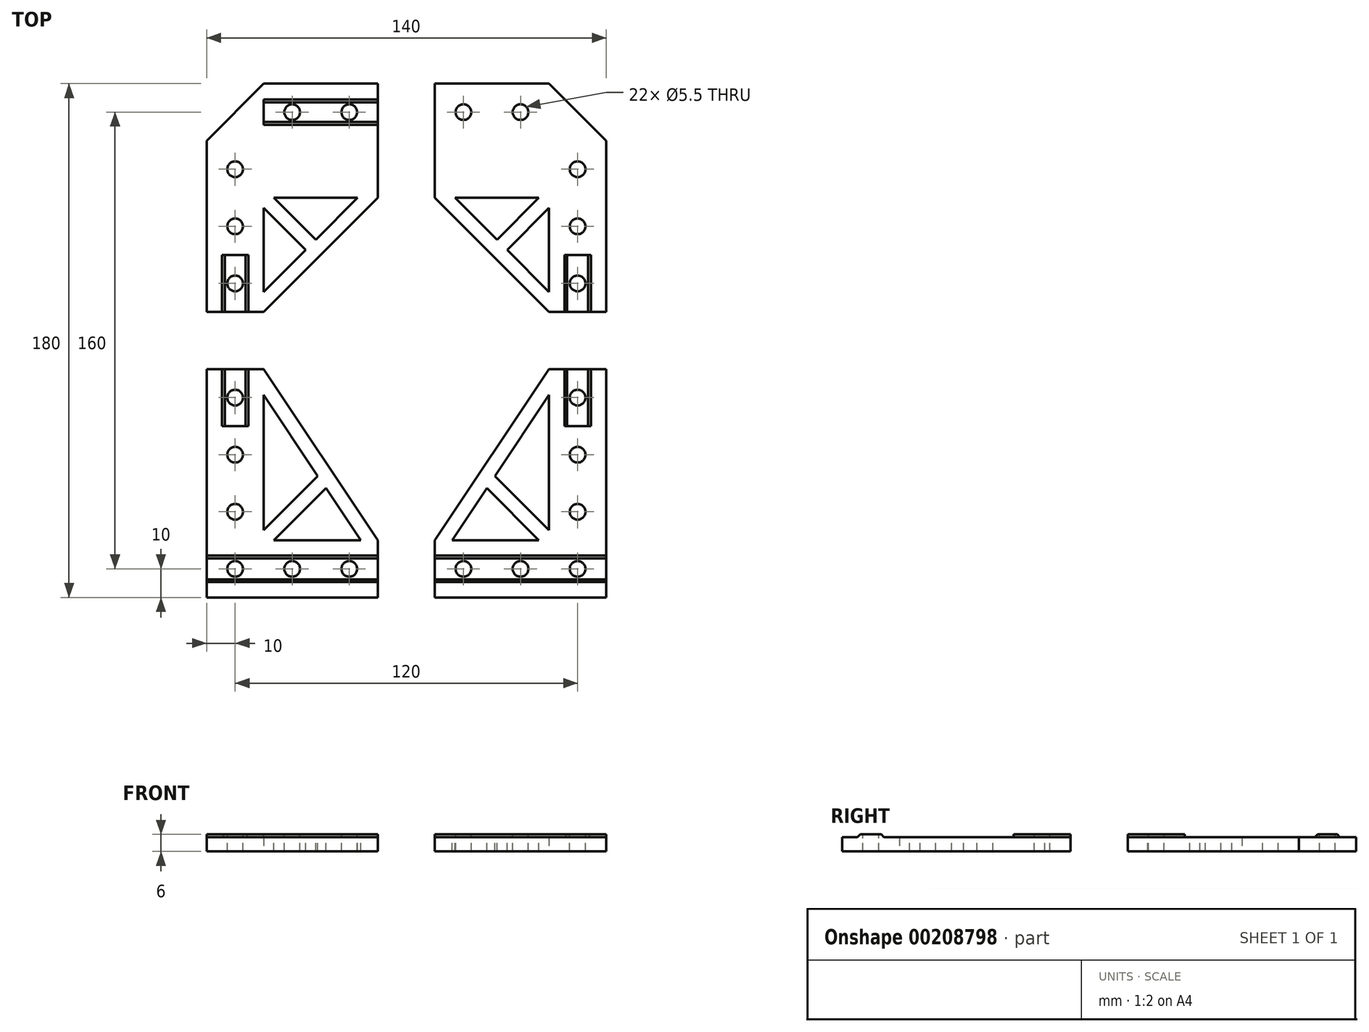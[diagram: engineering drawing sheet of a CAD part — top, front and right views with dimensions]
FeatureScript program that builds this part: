
annotation { "Feature Type Name" : "Feature", "Feature Type Description" : "" }
export const myFeature = defineFeature(function(context is Context, id is Id, definition is map)
    precondition{}
    {
        {
            var Q0;
            Q0=qCreatedBy(makeId("Top.planeOp"),FACE);
            var sketch = newSketch(context, id + "F0", { "sketchPlane" : qUnion([Q0])});
            skLineSegment(sketch, "E0", {"start": v(0, -60) * mm, "end": v(0, 0) * mm});
            skLineSegment(sketch, "E1", {"start": v(0, 0) * mm, "end": v(-20, 0) * mm, "construction": true});
            skLineSegment(sketch, "E2", {"start": v(-60, 0) * mm, "end": v(-60, -20) * mm});
            skLineSegment(sketch, "E3", {"start": v(-60, -20) * mm, "end": v(-20, -60) * mm});
            skLineSegment(sketch, "E4", {"start": v(-20, -60) * mm, "end": v(0, -60) * mm});
            skLineSegment(sketch, "E5", {"start": v(-60, 0) * mm, "end": v(-60, 20) * mm});
            skLineSegment(sketch, "E6", {"start": v(-60, 20) * mm, "end": v(-20, 20) * mm});
            skLineSegment(sketch, "E7", {"start": v(-20, 20) * mm, "end": v(-20, 0) * mm, "construction": true});
            skLineSegment(sketch, "E8", {"start": v(0, 0) * mm, "end": v(-20, 20) * mm});
            skLineSegment(sketch, "E9", {"start": v(-20, 10) * mm, "end": v(-30, 10) * mm, "construction": true});
            skLineSegment(sketch, "E10", {"start": v(-30, 10) * mm, "end": v(-50, 10) * mm, "construction": true});
            skLineSegment(sketch, "E11", {"start": v(-50, 10) * mm, "end": v(-60, 10) * mm, "construction": true});
            skLineSegment(sketch, "E12", {"start": v(-10, 0) * mm, "end": v(-10, -10) * mm, "construction": true});
            skPoint(sketch, "E12.endSnap0", {"position": v(-60, -10) * mm});
            skLineSegment(sketch, "E13", {"start": v(-10, -10) * mm, "end": v(-10, -30) * mm, "construction": true});
            skLineSegment(sketch, "E14", {"start": v(-10, -30) * mm, "end": v(-10, -50) * mm, "construction": true});
            skLineSegment(sketch, "E15", {"start": v(-10, -50) * mm, "end": v(-10, -60) * mm, "construction": true});
            skLineSegment(sketch, "E16", {"start": v(0, -80) * mm, "end": v(-20, -80) * mm});
            skLineSegment(sketch, "E17", {"start": v(-20, -80) * mm, "end": v(-60, -140) * mm});
            skLineSegment(sketch, "E18", {"start": v(-60, -140) * mm, "end": v(-60, -160) * mm});
            skLineSegment(sketch, "E19", {"start": v(-60, -160) * mm, "end": v(0, -160) * mm});
            skLineSegment(sketch, "E20", {"start": v(0, -160) * mm, "end": v(0, -80) * mm});
            skLineSegment(sketch, "E21", {"start": v(-60, -150) * mm, "end": v(-50, -150) * mm, "construction": true});
            skLineSegment(sketch, "E22", {"start": v(-50, -150) * mm, "end": v(-30, -150) * mm, "construction": true});
            skLineSegment(sketch, "E23", {"start": v(-30, -150) * mm, "end": v(-10, -150) * mm, "construction": true});
            skLineSegment(sketch, "E24", {"start": v(-10, -150) * mm, "end": v(0, -150) * mm, "construction": true});
            skLineSegment(sketch, "E25", {"start": v(-10, -80) * mm, "end": v(-10, -90) * mm, "construction": true});
            skLineSegment(sketch, "E26", {"start": v(-10, -90) * mm, "end": v(-10, -110) * mm, "construction": true});
            skLineSegment(sketch, "E27", {"start": v(-10, -110) * mm, "end": v(-10, -130) * mm, "construction": true});
            skLineSegment(sketch, "E28", {"start": v(-10, -130) * mm, "end": v(-10, -150) * mm, "construction": true});
            skLineSegment(sketch, "E29", {"start": v(-80, -160) * mm, "end": v(-80, -140) * mm});
            skLineSegment(sketch, "E30", {"start": v(-80, -140) * mm, "end": v(-120, -80) * mm});
            skLineSegment(sketch, "E31", {"start": v(-120, -80) * mm, "end": v(-140, -80) * mm});
            skLineSegment(sketch, "E32", {"start": v(-140, -80) * mm, "end": v(-140, -160) * mm});
            skLineSegment(sketch, "E33", {"start": v(-140, -160) * mm, "end": v(-80, -160) * mm});
            skLineSegment(sketch, "E34", {"start": v(-120, -60) * mm, "end": v(-140, -60) * mm});
            skLineSegment(sketch, "E35", {"start": v(-140, -60) * mm, "end": v(-140, 0) * mm});
            skLineSegment(sketch, "E36", {"start": v(-140, 0) * mm, "end": v(-120, 20) * mm});
            skLineSegment(sketch, "E37", {"start": v(-120, 20) * mm, "end": v(-80, 20) * mm});
            skLineSegment(sketch, "E38", {"start": v(-80, -20) * mm, "end": v(-120, -60) * mm});
            skLineSegment(sketch, "E39", {"start": v(-80, 20) * mm, "end": v(-80, 0) * mm});
            skLineSegment(sketch, "E40", {"start": v(-80, 0) * mm, "end": v(-80, -20) * mm});
            skLineSegment(sketch, "E41", {"start": v(-140, 0) * mm, "end": v(-120, 0) * mm, "construction": true});
            skLineSegment(sketch, "E42", {"start": v(-120, 0) * mm, "end": v(-120, 20) * mm, "construction": true});
            skLineSegment(sketch, "E43", {"start": v(-120, 10) * mm, "end": v(-110, 10) * mm, "construction": true});
            skLineSegment(sketch, "E44", {"start": v(-110, 10) * mm, "end": v(-90, 10) * mm, "construction": true});
            skLineSegment(sketch, "E45", {"start": v(-90, 10) * mm, "end": v(-80, 10) * mm, "construction": true});
            skLineSegment(sketch, "E46", {"start": v(-130, -10) * mm, "end": v(-130, -30) * mm, "construction": true});
            skLineSegment(sketch, "E47", {"start": v(-130, -30) * mm, "end": v(-130, -50) * mm, "construction": true});
            skLineSegment(sketch, "E48", {"start": v(-130, -50) * mm, "end": v(-130, -60) * mm, "construction": true});
            skLineSegment(sketch, "E49", {"start": v(-80, -150) * mm, "end": v(-90, -150) * mm, "construction": true});
            skLineSegment(sketch, "E50", {"start": v(-90, -150) * mm, "end": v(-110, -150) * mm, "construction": true});
            skLineSegment(sketch, "E51", {"start": v(-110, -150) * mm, "end": v(-130, -150) * mm, "construction": true});
            skLineSegment(sketch, "E52", {"start": v(-130, -150) * mm, "end": v(-130, -130) * mm, "construction": true});
            skLineSegment(sketch, "E53", {"start": v(-130, -130) * mm, "end": v(-130, -110) * mm, "construction": true});
            skLineSegment(sketch, "E54", {"start": v(-130, -110) * mm, "end": v(-130, -90) * mm, "construction": true});
            skLineSegment(sketch, "E55", {"start": v(-130, -90) * mm, "end": v(-130, -80) * mm, "construction": true});
            skLineSegment(sketch, "E56", {"start": v(-130, -10) * mm, "end": v(-130, 0) * mm});
            skSolve(sketch);
        }
        {
            var Q0;
            Q0=makeQuery(id+"F0.imprint","IMPRINT",FACE,{"disambiguationData":[TD([[makeQuery(id+"F0.imprint","IMPRINT",EDGE,{"derivedFrom":sQuery(id+"F0.wireOp",EDGE,"E0")}),1.0]])]});
            var Q1;
            Q1=makeQuery(id+"F0.imprint","IMPRINT",FACE,{"disambiguationData":[TD([[makeQuery(id+"F0.imprint","IMPRINT",EDGE,{"derivedFrom":sQuery(id+"F0.wireOp",EDGE,"E16")}),1.0]])]});
            var Q2;
            Q2=makeQuery(id+"F0.imprint","IMPRINT",FACE,{"disambiguationData":[TD([[makeQuery(id+"F0.imprint","IMPRINT",EDGE,{"derivedFrom":sQuery(id+"F0.wireOp",EDGE,"E34")}),-1.0]])]});
            var Q3;
            Q3=makeQuery(id+"F0.imprint","IMPRINT",FACE,{"disambiguationData":[TD([[makeQuery(id+"F0.imprint","IMPRINT",EDGE,{"derivedFrom":sQuery(id+"F0.wireOp",EDGE,"E29")}),1.0]])]});
            extrude(context, id + "F1", {"entities" : qUnion([Q0, Q1, Q2, Q3]), "depth" : 5 * mm});
        }
        {
            var Q0;
            Q0=makeQuery(id+"F1.opExtrude","CAP_FACE",FACE,{"disambiguationData":[OSD([sQuery(id+"F0.wireOp",EDGE,"E0"),sQuery(id+"F0.wireOp",EDGE,"E2"),sQuery(id+"F0.wireOp",EDGE,"E3"),sQuery(id+"F0.wireOp",EDGE,"E4"),sQuery(id+"F0.wireOp",EDGE,"E5"),sQuery(id+"F0.wireOp",EDGE,"E6"),sQuery(id+"F0.wireOp",EDGE,"E8")])],"isStart":false});
            var sketch = newSketch(context, id + "F2", { "sketchPlane" : qUnion([Q0])});
            skLineSegment(sketch, "E57", {"start": v(-23.54, -20) * mm, "end": v(-52.93, -20) * mm});
            skLineSegment(sketch, "E58", {"start": v(-52.93, -20) * mm, "end": v(-38.23, -34.7) * mm});
            skLineSegment(sketch, "E59", {"start": v(-38.23, -34.7) * mm, "end": v(-23.54, -20) * mm});
            skLineSegment(sketch, "E60", {"start": v(-20, -23.54) * mm, "end": v(-34.7, -38.23) * mm});
            skLineSegment(sketch, "E61", {"start": v(-34.7, -38.23) * mm, "end": v(-20, -52.93) * mm});
            skLineSegment(sketch, "E62", {"start": v(-20, -52.93) * mm, "end": v(-20, -23.54) * mm});
            skLineSegment(sketch, "E63", {"start": v(-23.54, -20) * mm, "end": v(-20, -20) * mm, "construction": true});
            skLineSegment(sketch, "E64", {"start": v(-20, -20) * mm, "end": v(-20, -23.54) * mm, "construction": true});
            skSolve(sketch);
        }
        {
            var Q0;
            Q0=makeQuery(id+"F2.imprint","IMPRINT",FACE,{"disambiguationData":[TD([[makeQuery(id+"F2.imprint","IMPRINT",EDGE,{"derivedFrom":sQuery(id+"F2.wireOp",EDGE,"E57")}),1.0]])]});
            var Q1;
            Q1=makeQuery(id+"F2.imprint","IMPRINT",FACE,{"disambiguationData":[TD([[makeQuery(id+"F2.imprint","IMPRINT",EDGE,{"derivedFrom":sQuery(id+"F2.wireOp",EDGE,"E60")}),1.0]])]});
            var Q2;
            Q2=sQuery(id+"F2.wireOp",EDGE,"YBFqt27e-qfMf-Dqdc-nEIm-QrJc93Nj7R85");
            var Q3;
            Q3=sQuery(id+"F2.wireOp",EDGE,"gDKsQo0I-stO4-j41u-VVKn-dd11EjwDGm8N");
            extrude(context, id + "F3", {"entities" : qUnion([Q0, Q1]), "operationType" : NewBodyOperationType.REMOVE, "surfaceEntities" : qUnion([Q2, Q3]), "endBound" : BoundingType.THROUGH_ALL, "oppositeDirection" : true, "depth" : 25 * mm});
        }
        {
            var Q0;
            Q0=makeQuery(id+"F1.opExtrude","SWEPT_FACE",FACE,{"disambiguationData":[OSD([sQuery(id+"F0.wireOp",EDGE,"E4")])]});
            var sketch = newSketch(context, id + "F4", { "sketchPlane" : qUnion([Q0])});
            skLineSegment(sketch, "E65", {"start": v(-20, 5) * mm, "end": v(-14.64, 5) * mm, "construction": true});
            skLineSegment(sketch, "E66", {"start": v(-14.64, 5) * mm, "end": v(-5.36, 5) * mm});
            skLineSegment(sketch, "E67", {"start": v(-5.36, 5) * mm, "end": v(0, 5) * mm, "construction": true});
            skLineSegment(sketch, "E68", {"start": v(-6.36, 6) * mm, "end": v(-5.36, 5) * mm});
            skLineSegment(sketch, "E69", {"start": v(-7.16, 6.8) * mm, "end": v(-6.36, 6) * mm, "construction": true});
            skLineSegment(sketch, "E70", {"start": v(-10, 9.64) * mm, "end": v(-7.16, 6.8) * mm, "construction": true});
            skLineSegment(sketch, "E71", {"start": v(-12.84, 6.8) * mm, "end": v(-10, 9.64) * mm, "construction": true});
            skLineSegment(sketch, "E72", {"start": v(-13.64, 6) * mm, "end": v(-12.84, 6.8) * mm, "construction": true});
            skLineSegment(sketch, "E73", {"start": v(-14.64, 5) * mm, "end": v(-13.64, 6) * mm});
            skLineSegment(sketch, "E74", {"start": v(-13.64, 6) * mm, "end": v(-6.36, 6) * mm});
            skLineSegment(sketch, "E75", {"start": v(-12.84, 6.8) * mm, "end": v(-7.16, 6.8) * mm, "construction": true});
            skLineSegment(sketch, "E76", {"start": v(-10, 6) * mm, "end": v(-10, 5) * mm, "construction": true});
            skSolve(sketch);
        }
        {
            var Q0;
            Q0=makeQuery(id+"F4.imprint","IMPRINT",FACE,{"disambiguationData":[TD([[makeQuery(id+"F4.imprint","IMPRINT",EDGE,{"derivedFrom":sQuery(id+"F4.wireOp",EDGE,"E66")}),1.0]])]});
            var Q1;
            Q1=sQuery(id+"F4.wireOp",EDGE,"E71");
            var Q2;
            Q2=sQuery(id+"F4.wireOp",EDGE,"E70");
            var Q3;
            Q3=sQuery(id+"F4.wireOp",EDGE,"E67");
            var Q4;
            Q4=sQuery(id+"F4.wireOp",EDGE,"E65");
            var Q5;
            Q5=sQuery(id+"F4.wireOp",EDGE,"E72");
            var Q6;
            Q6=sQuery(id+"F4.wireOp",EDGE,"E75");
            var Q7;
            Q7=sQuery(id+"F4.wireOp",EDGE,"E69");
            var Q8;
            Q8=sQuery(id+"F4.wireOp",EDGE,"E76");
            var Q9;
            Q9=makeQuery(id+"F1.opExtrude","SWEPT_FACE",FACE,{"disambiguationData":[OSD([sQuery(id+"F0.wireOp",EDGE,"E8")])]});
            extrude(context, id + "F5", {"entities" : qUnion([Q0]), "operationType" : NewBodyOperationType.ADD, "surfaceEntities" : qUnion([Q1, Q2, Q3, Q4, Q5, Q6, Q7, Q8]), "oppositeDirection" : true, "endBoundEntityFace" : qUnion([Q9]), "depth" : 20 * mm});
        }
        {
            var Q0;
            Q0=makeQuery(id+"F1.opExtrude","SWEPT_FACE",FACE,{"disambiguationData":[OSD([sQuery(id+"F0.wireOp",EDGE,"E2"),sQuery(id+"F0.wireOp",EDGE,"E5")])]});
            var sketch = newSketch(context, id + "F6", { "sketchPlane" : qUnion([Q0])});
            skLineSegment(sketch, "E77", {"start": v(-20, 5) * mm, "end": v(-14.64, 5) * mm, "construction": true});
            skLineSegment(sketch, "E78", {"start": v(-14.64, 5) * mm, "end": v(-5.36, 5) * mm});
            skLineSegment(sketch, "E79", {"start": v(-5.36, 5) * mm, "end": v(-6.36, 6) * mm});
            skLineSegment(sketch, "E80", {"start": v(-6.36, 6) * mm, "end": v(-7.16, 6.8) * mm, "construction": true});
            skLineSegment(sketch, "E81", {"start": v(-7.16, 6.8) * mm, "end": v(-10, 9.64) * mm, "construction": true});
            skLineSegment(sketch, "E82", {"start": v(-10, 9.64) * mm, "end": v(-12.84, 6.8) * mm, "construction": true});
            skLineSegment(sketch, "E83", {"start": v(-12.84, 6.8) * mm, "end": v(-13.64, 6) * mm, "construction": true});
            skLineSegment(sketch, "E84", {"start": v(-13.64, 6) * mm, "end": v(-14.64, 5) * mm});
            skLineSegment(sketch, "E85", {"start": v(-6.36, 6) * mm, "end": v(-13.64, 6) * mm});
            skLineSegment(sketch, "E86", {"start": v(-12.84, 6.8) * mm, "end": v(-7.16, 6.8) * mm, "construction": true});
            skLineSegment(sketch, "E87", {"start": v(-10, 6) * mm, "end": v(-10, 5) * mm, "construction": true});
            skSolve(sketch);
        }
        {
            var Q0;
            Q0=makeQuery(id+"F6.imprint","IMPRINT",FACE,{"disambiguationData":[TD([[makeQuery(id+"F6.imprint","IMPRINT",EDGE,{"derivedFrom":sQuery(id+"F6.wireOp",EDGE,"E78")}),-1.0]])]});
            var Q1;
            Q1=sQuery(id+"F6.wireOp",EDGE,"E82");
            var Q2;
            Q2=sQuery(id+"F6.wireOp",EDGE,"E81");
            var Q3;
            Q3=sQuery(id+"F6.wireOp",EDGE,"E86");
            var Q4;
            Q4=sQuery(id+"F6.wireOp",EDGE,"E80");
            var Q5;
            Q5=sQuery(id+"F6.wireOp",EDGE,"E83");
            var Q6;
            Q6=sQuery(id+"F6.wireOp",EDGE,"E77");
            var Q7;
            Q7=sQuery(id+"F6.wireOp",EDGE,"E87");
            extrude(context, id + "F7", {"entities" : qUnion([Q0]), "operationType" : NewBodyOperationType.ADD, "surfaceEntities" : qUnion([Q1, Q2, Q3, Q4, Q5, Q6, Q7]), "oppositeDirection" : true, "depth" : 40 * mm});
        }
        {
            var Q0;
            Q0=makeQuery(id+"F1.opExtrude","SWEPT_FACE",FACE,{"disambiguationData":[OSD([sQuery(id+"F0.wireOp",EDGE,"E16")])]});
            var sketch = newSketch(context, id + "F8", { "sketchPlane" : qUnion([Q0])});
            skLineSegment(sketch, "E88", {"start": v(0, 5) * mm, "end": v(5.36, 5) * mm, "construction": true});
            skLineSegment(sketch, "E89", {"start": v(14.64, 5) * mm, "end": v(20, 5) * mm, "construction": true});
            skLineSegment(sketch, "E90", {"start": v(5.36, 5) * mm, "end": v(14.64, 5) * mm});
            skLineSegment(sketch, "E91", {"start": v(10, 5) * mm, "end": v(10, 0) * mm, "construction": true});
            skLineSegment(sketch, "E92", {"start": v(5.36, 5) * mm, "end": v(6.36, 6) * mm});
            skLineSegment(sketch, "E93", {"start": v(6.36, 6) * mm, "end": v(7.16, 6.8) * mm, "construction": true});
            skLineSegment(sketch, "E94", {"start": v(7.16, 6.8) * mm, "end": v(10, 9.64) * mm, "construction": true});
            skLineSegment(sketch, "E95", {"start": v(10, 9.64) * mm, "end": v(12.84, 6.8) * mm, "construction": true});
            skLineSegment(sketch, "E96", {"start": v(12.84, 6.8) * mm, "end": v(13.64, 6) * mm, "construction": true});
            skLineSegment(sketch, "E97", {"start": v(13.64, 6) * mm, "end": v(14.64, 5) * mm});
            skLineSegment(sketch, "E98", {"start": v(6.36, 6) * mm, "end": v(13.64, 6) * mm});
            skLineSegment(sketch, "E99", {"start": v(7.16, 6.8) * mm, "end": v(12.84, 6.8) * mm, "construction": true});
            skLineSegment(sketch, "E100", {"start": v(10, 5) * mm, "end": v(10, 6) * mm, "construction": true});
            skSolve(sketch);
        }
        {
            var Q0;
            Q0=qSketchRegion(id+"F8",true);
            var Q1;
            Q1=sQuery(id+"F8.wireOp",EDGE,"E100");
            var Q2;
            Q2=sQuery(id+"F8.wireOp",EDGE,"E88");
            var Q3;
            Q3=sQuery(id+"F8.wireOp",EDGE,"E91");
            var Q4;
            Q4=sQuery(id+"F8.wireOp",EDGE,"E89");
            var Q5;
            Q5=sQuery(id+"F8.wireOp",EDGE,"E96");
            var Q6;
            Q6=sQuery(id+"F8.wireOp",EDGE,"E99");
            var Q7;
            Q7=sQuery(id+"F8.wireOp",EDGE,"E95");
            var Q8;
            Q8=sQuery(id+"F8.wireOp",EDGE,"E94");
            var Q9;
            Q9=sQuery(id+"F8.wireOp",EDGE,"E93");
            extrude(context, id + "F9", {"entities" : qUnion([Q0]), "operationType" : NewBodyOperationType.ADD, "surfaceEntities" : qUnion([Q1, Q2, Q3, Q4, Q5, Q6, Q7, Q8, Q9]), "oppositeDirection" : true, "depth" : 20 * mm});
        }
        {
            var Q0;
            Q0=makeQuery(id+"F1.opExtrude","SWEPT_FACE",FACE,{"disambiguationData":[OSD([sQuery(id+"F0.wireOp",EDGE,"E20")])]});
            var sketch = newSketch(context, id + "F10", { "sketchPlane" : qUnion([Q0])});
            skLineSegment(sketch, "E101", {"start": v(-160, 5) * mm, "end": v(-154.64, 5) * mm, "construction": true});
            skLineSegment(sketch, "E102", {"start": v(-154.64, 5) * mm, "end": v(-145.36, 5) * mm});
            skLineSegment(sketch, "E103", {"start": v(-145.36, 5) * mm, "end": v(-140, 5) * mm, "construction": true});
            skLineSegment(sketch, "E104", {"start": v(-150, 5) * mm, "end": v(-150, 0) * mm, "construction": true});
            skLineSegment(sketch, "E105", {"start": v(-154.64, 5) * mm, "end": v(-153.64, 6) * mm});
            skLineSegment(sketch, "E106", {"start": v(-153.64, 6) * mm, "end": v(-152.84, 6.8) * mm, "construction": true});
            skLineSegment(sketch, "E107", {"start": v(-152.84, 6.8) * mm, "end": v(-150, 9.64) * mm, "construction": true});
            skLineSegment(sketch, "E108", {"start": v(-150, 9.64) * mm, "end": v(-147.16, 6.8) * mm, "construction": true});
            skLineSegment(sketch, "E109", {"start": v(-147.16, 6.8) * mm, "end": v(-146.36, 6) * mm, "construction": true});
            skLineSegment(sketch, "E110", {"start": v(-146.36, 6) * mm, "end": v(-145.36, 5) * mm});
            skLineSegment(sketch, "E111", {"start": v(-152.84, 6.8) * mm, "end": v(-147.16, 6.8) * mm, "construction": true});
            skLineSegment(sketch, "E112", {"start": v(-153.64, 6) * mm, "end": v(-146.36, 6) * mm});
            skLineSegment(sketch, "E113", {"start": v(-150, 6) * mm, "end": v(-150, 5) * mm, "construction": true});
            skSolve(sketch);
        }
        {
            var Q0;
            Q0=makeQuery(id+"F10.imprint","IMPRINT",FACE,{"disambiguationData":[TD([[makeQuery(id+"F10.imprint","IMPRINT",EDGE,{"derivedFrom":sQuery(id+"F10.wireOp",EDGE,"E102")}),1.0]])]});
            var Q1;
            Q1=makeQuery(id+"F1.opExtrude","SWEPT_FACE",FACE,{"disambiguationData":[OSD([sQuery(id+"F0.wireOp",EDGE,"E18")])]});
            extrude(context, id + "F11", {"entities" : qUnion([Q0]), "operationType" : NewBodyOperationType.ADD, "endBound" : BoundingType.UP_TO_SURFACE, "oppositeDirection" : true, "endBoundEntityFace" : qUnion([Q1]), "depth" : 25 * mm});
        }
        {
            var Q0;
            {var subQ4=sQuery(id+"F0.wireOp",EDGE,"E16");var subQ9=sQuery(id+"F0.wireOp",EDGE,"E17");var subQ10=sQuery(id+"F0.wireOp",EDGE,"E18");var subQ11=sQuery(id+"F0.wireOp",EDGE,"E20");Q0=makeQuery(id+"F11.boolean.opBoolean","SPLIT",FACE,{"disambiguationData":[TD([makeQuery(id+"F1.opExtrude","SWEPT_FACE",FACE,{"disambiguationData":[OSD([subQ4])]})])],"derivedFrom":makeQuery(id+"F1.opExtrude","CAP_FACE",FACE,{"disambiguationData":[OSD([subQ4,subQ9,subQ10,sQuery(id+"F0.wireOp",EDGE,"E19"),subQ11])],"isStart":false})});}
            var sketch = newSketch(context, id + "F12", { "sketchPlane" : qUnion([Q0])});
            skLineSegment(sketch, "E114", {"start": v(-54, -140) * mm, "end": v(-23.54, -140) * mm});
            skLineSegment(sketch, "E115", {"start": v(-23.54, -140) * mm, "end": v(-41.8, -121.73) * mm});
            skLineSegment(sketch, "E116", {"start": v(-41.8, -121.73) * mm, "end": v(-54, -140) * mm});
            skLineSegment(sketch, "E117", {"start": v(-20, -136.46) * mm, "end": v(-38.98, -117.48) * mm});
            skLineSegment(sketch, "E118", {"start": v(-38.98, -117.48) * mm, "end": v(-20, -89.01) * mm});
            skLineSegment(sketch, "E119", {"start": v(-20, -89.01) * mm, "end": v(-20, -136.46) * mm});
            skLineSegment(sketch, "E120", {"start": v(-23.54, -140) * mm, "end": v(-20, -140) * mm, "construction": true});
            skLineSegment(sketch, "E121", {"start": v(-20, -140) * mm, "end": v(-20, -136.46) * mm, "construction": true});
            skSolve(sketch);
        }
        {
            var Q0;
            Q0=makeQuery(id+"F12.imprint","IMPRINT",FACE,{"disambiguationData":[TD([[makeQuery(id+"F12.imprint","IMPRINT",EDGE,{"derivedFrom":sQuery(id+"F12.wireOp",EDGE,"E117")}),-1.0]])]});
            var Q1;
            Q1=makeQuery(id+"F12.imprint","IMPRINT",FACE,{"disambiguationData":[TD([[makeQuery(id+"F12.imprint","IMPRINT",EDGE,{"derivedFrom":sQuery(id+"F12.wireOp",EDGE,"E114")}),1.0]])]});
            extrude(context, id + "F13", {"entities" : qUnion([Q0, Q1]), "operationType" : NewBodyOperationType.REMOVE, "oppositeDirection" : true, "depth" : 25 * mm});
        }
        {
            var Q0;
            Q0=makeQuery(id+"F1.opExtrude","SWEPT_FACE",FACE,{"disambiguationData":[OSD([sQuery(id+"F0.wireOp",EDGE,"E32")])]});
            var sketch = newSketch(context, id + "F14", { "sketchPlane" : qUnion([Q0])});
            skLineSegment(sketch, "E122", {"start": v(145.36, 5) * mm, "end": v(154.64, 5) * mm});
            skLineSegment(sketch, "E123", {"start": v(154.64, 5) * mm, "end": v(153.64, 6) * mm});
            skLineSegment(sketch, "E124", {"start": v(153.64, 6) * mm, "end": v(152.84, 6.8) * mm, "construction": true});
            skLineSegment(sketch, "E125", {"start": v(152.84, 6.8) * mm, "end": v(150, 9.64) * mm, "construction": true});
            skLineSegment(sketch, "E126", {"start": v(150, 9.64) * mm, "end": v(147.16, 6.8) * mm, "construction": true});
            skLineSegment(sketch, "E127", {"start": v(147.16, 6.8) * mm, "end": v(146.36, 6) * mm, "construction": true});
            skLineSegment(sketch, "E128", {"start": v(146.36, 6) * mm, "end": v(145.36, 5) * mm});
            skLineSegment(sketch, "E129", {"start": v(146.36, 6) * mm, "end": v(153.64, 6) * mm});
            skLineSegment(sketch, "E130", {"start": v(152.84, 6.8) * mm, "end": v(147.16, 6.8) * mm, "construction": true});
            skLineSegment(sketch, "E131", {"start": v(150, 0) * mm, "end": v(150, 5) * mm, "construction": true});
            skLineSegment(sketch, "E132", {"start": v(150, 6) * mm, "end": v(150, 5) * mm, "construction": true});
            skSolve(sketch);
        }
        {
            var Q0;
            Q0=makeQuery(id+"F14.imprint","IMPRINT",FACE,{"disambiguationData":[TD([[makeQuery(id+"F14.imprint","IMPRINT",EDGE,{"derivedFrom":sQuery(id+"F14.wireOp",EDGE,"E122")}),1.0]])]});
            var Q1;
            Q1=makeQuery(id+"F1.opExtrude","SWEPT_FACE",FACE,{"disambiguationData":[OSD([sQuery(id+"F0.wireOp",EDGE,"E29")])]});
            extrude(context, id + "F15", {"entities" : qUnion([Q0]), "operationType" : NewBodyOperationType.ADD, "endBound" : BoundingType.UP_TO_SURFACE, "oppositeDirection" : true, "endBoundEntityFace" : qUnion([Q1]), "depth" : 25 * mm});
        }
        {
            var Q0;
            Q0=makeQuery(id+"F1.opExtrude","SWEPT_FACE",FACE,{"disambiguationData":[OSD([sQuery(id+"F0.wireOp",EDGE,"E31")])]});
            var sketch = newSketch(context, id + "F16", { "sketchPlane" : qUnion([Q0])});
            skLineSegment(sketch, "E133", {"start": v(134.64, 5) * mm, "end": v(125.36, 5) * mm});
            skLineSegment(sketch, "E134", {"start": v(125.36, 5) * mm, "end": v(126.36, 6) * mm});
            skLineSegment(sketch, "E135", {"start": v(126.36, 6) * mm, "end": v(127.16, 6.8) * mm, "construction": true});
            skLineSegment(sketch, "E136", {"start": v(127.16, 6.8) * mm, "end": v(130, 9.64) * mm, "construction": true});
            skLineSegment(sketch, "E137", {"start": v(130, 9.64) * mm, "end": v(132.84, 6.8) * mm, "construction": true});
            skLineSegment(sketch, "E138", {"start": v(132.84, 6.8) * mm, "end": v(133.64, 6) * mm, "construction": true});
            skLineSegment(sketch, "E139", {"start": v(133.64, 6) * mm, "end": v(134.64, 5) * mm});
            skLineSegment(sketch, "E140", {"start": v(130, 5) * mm, "end": v(130, 0) * mm, "construction": true});
            skLineSegment(sketch, "E141", {"start": v(126.36, 6) * mm, "end": v(133.64, 6) * mm});
            skLineSegment(sketch, "E142", {"start": v(132.84, 6.8) * mm, "end": v(127.16, 6.8) * mm, "construction": true});
            skLineSegment(sketch, "E143", {"start": v(130, 6) * mm, "end": v(130, 5) * mm, "construction": true});
            skSolve(sketch);
        }
        {
            var Q0;
            Q0=makeQuery(id+"F16.imprint","IMPRINT",FACE,{"disambiguationData":[TD([[makeQuery(id+"F16.imprint","IMPRINT",EDGE,{"derivedFrom":sQuery(id+"F16.wireOp",EDGE,"E133")}),1.0]])]});
            extrude(context, id + "F17", {"entities" : qUnion([Q0]), "operationType" : NewBodyOperationType.ADD, "oppositeDirection" : true, "depth" : 20 * mm});
        }
        {
            var Q0;
            Q0=makeQuery(id+"F1.opExtrude","SWEPT_FACE",FACE,{"disambiguationData":[OSD([sQuery(id+"F0.wireOp",EDGE,"E34")])]});
            var sketch = newSketch(context, id + "F18", { "sketchPlane" : qUnion([Q0])});
            skLineSegment(sketch, "E144", {"start": v(-134.64, 5) * mm, "end": v(-125.36, 5) * mm});
            skLineSegment(sketch, "E145", {"start": v(-125.36, 5) * mm, "end": v(-126.36, 6) * mm});
            skLineSegment(sketch, "E146", {"start": v(-126.36, 6) * mm, "end": v(-127.16, 6.8) * mm, "construction": true});
            skLineSegment(sketch, "E147", {"start": v(-127.16, 6.8) * mm, "end": v(-130, 9.64) * mm, "construction": true});
            skLineSegment(sketch, "E148", {"start": v(-130, 9.64) * mm, "end": v(-132.84, 6.8) * mm, "construction": true});
            skLineSegment(sketch, "E149", {"start": v(-132.84, 6.8) * mm, "end": v(-133.64, 6) * mm, "construction": true});
            skLineSegment(sketch, "E150", {"start": v(-133.64, 6) * mm, "end": v(-134.64, 5) * mm});
            skLineSegment(sketch, "E151", {"start": v(-127.16, 6.8) * mm, "end": v(-132.84, 6.8) * mm, "construction": true});
            skLineSegment(sketch, "E152", {"start": v(-133.64, 6) * mm, "end": v(-126.36, 6) * mm});
            skLineSegment(sketch, "E153", {"start": v(-130, 5) * mm, "end": v(-130, 6) * mm, "construction": true});
            skLineSegment(sketch, "E154", {"start": v(-130, 5) * mm, "end": v(-130, 0) * mm, "construction": true});
            skSolve(sketch);
        }
        {
            var Q0;
            Q0=makeQuery(id+"F18.imprint","IMPRINT",FACE,{"disambiguationData":[TD([[makeQuery(id+"F18.imprint","IMPRINT",EDGE,{"derivedFrom":sQuery(id+"F18.wireOp",EDGE,"E144")}),-1.0]])]});
            var Q1;
            Q1=sQuery(id+"F18.wireOp",EDGE,"E154");
            var Q2;
            Q2=sQuery(id+"F18.wireOp",EDGE,"E153");
            var Q3;
            Q3=sQuery(id+"F18.wireOp",EDGE,"E149");
            var Q4;
            Q4=sQuery(id+"F18.wireOp",EDGE,"E151");
            var Q5;
            Q5=sQuery(id+"F18.wireOp",EDGE,"E146");
            var Q6;
            Q6=sQuery(id+"F18.wireOp",EDGE,"E147");
            var Q7;
            Q7=sQuery(id+"F18.wireOp",EDGE,"E148");
            extrude(context, id + "F19", {"entities" : qUnion([Q0]), "operationType" : NewBodyOperationType.ADD, "surfaceEntities" : qUnion([Q1, Q2, Q3, Q4, Q5, Q6, Q7]), "oppositeDirection" : true, "depth" : 20 * mm});
        }
        {
            var Q0;
            Q0=makeQuery(id+"F1.opExtrude","SWEPT_FACE",FACE,{"disambiguationData":[OSD([sQuery(id+"F0.wireOp",EDGE,"E39"),sQuery(id+"F0.wireOp",EDGE,"E40")])]});
            var sketch = newSketch(context, id + "F20", { "sketchPlane" : qUnion([Q0])});
            skLineSegment(sketch, "E155", {"start": v(5.6, 5) * mm, "end": v(14.4, 5) * mm});
            skLineSegment(sketch, "E156", {"start": v(14.4, 5) * mm, "end": v(13.4, 6) * mm});
            skLineSegment(sketch, "E157", {"start": v(13.4, 6) * mm, "end": v(12.6, 6.8) * mm, "construction": true});
            skLineSegment(sketch, "E158", {"start": v(12.6, 6.8) * mm, "end": v(10, 9.4) * mm, "construction": true});
            skLineSegment(sketch, "E159", {"start": v(10, 9.4) * mm, "end": v(7.4, 6.8) * mm, "construction": true});
            skLineSegment(sketch, "E160", {"start": v(7.4, 6.8) * mm, "end": v(6.6, 6) * mm, "construction": true});
            skLineSegment(sketch, "E161", {"start": v(6.6, 6) * mm, "end": v(5.6, 5) * mm});
            skLineSegment(sketch, "E162", {"start": v(10, 5) * mm, "end": v(10, 0) * mm, "construction": true});
            skLineSegment(sketch, "E163", {"start": v(13.4, 6) * mm, "end": v(6.6, 6) * mm});
            skLineSegment(sketch, "E164", {"start": v(7.4, 6.8) * mm, "end": v(12.6, 6.8) * mm, "construction": true});
            skLineSegment(sketch, "E165", {"start": v(10, 6) * mm, "end": v(10, 5) * mm, "construction": true});
            skSolve(sketch);
        }
        {
            var Q0;
            Q0=makeQuery(id+"F20.imprint","IMPRINT",FACE,{"disambiguationData":[TD([[makeQuery(id+"F20.imprint","IMPRINT",EDGE,{"derivedFrom":sQuery(id+"F20.wireOp",EDGE,"E155")}),-1.0]])]});
            var Q1;
            Q1=sQuery(id+"F20.wireOp",EDGE,"E165");
            var Q2;
            Q2=sQuery(id+"F20.wireOp",EDGE,"E162");
            var Q3;
            Q3=sQuery(id+"F20.wireOp",EDGE,"E160");
            var Q4;
            Q4=sQuery(id+"F20.wireOp",EDGE,"E164");
            var Q5;
            Q5=sQuery(id+"F20.wireOp",EDGE,"E159");
            var Q6;
            Q6=sQuery(id+"F20.wireOp",EDGE,"E158");
            var Q7;
            Q7=sQuery(id+"F20.wireOp",EDGE,"E157");
            extrude(context, id + "F21", {"entities" : qUnion([Q0]), "operationType" : NewBodyOperationType.ADD, "surfaceEntities" : qUnion([Q1, Q2, Q3, Q4, Q5, Q6, Q7]), "oppositeDirection" : true, "depth" : 40 * mm});
        }
        {
            var Q0;
            Q0=sQuery(id+"F0.wireOp",VERTEX,"E44.start");
            var Q1;
            Q1=sQuery(id+"F0.wireOp",VERTEX,"E44.end");
            var Q2;
            Q2=sQuery(id+"F0.wireOp",VERTEX,"E11.start");
            var Q3;
            Q3=sQuery(id+"F0.wireOp",VERTEX,"E10.start");
            var Q4;
            Q4=sQuery(id+"F0.wireOp",VERTEX,"E46.start");
            var Q5;
            Q5=sQuery(id+"F0.wireOp",VERTEX,"E12.end");
            var Q6;
            Q6=sQuery(id+"F0.wireOp",VERTEX,"E14.start");
            var Q7;
            Q7=sQuery(id+"F0.wireOp",VERTEX,"E15.start");
            var Q8;
            Q8=sQuery(id+"F0.wireOp",VERTEX,"E47.end");
            var Q9;
            Q9=sQuery(id+"F0.wireOp",VERTEX,"E47.start");
            var Q10;
            Q10=sQuery(id+"F0.wireOp",VERTEX,"E52.end");
            var Q11;
            Q11=sQuery(id+"F0.wireOp",VERTEX,"E53.end");
            var Q12;
            Q12=sQuery(id+"F0.wireOp",VERTEX,"E55.start");
            var Q13;
            Q13=sQuery(id+"F0.wireOp",VERTEX,"E28.start");
            var Q14;
            Q14=sQuery(id+"F0.wireOp",VERTEX,"E27.start");
            var Q15;
            Q15=sQuery(id+"F0.wireOp",VERTEX,"E26.start");
            var Q16;
            Q16=sQuery(id+"F0.wireOp",VERTEX,"E52.start");
            var Q17;
            Q17=sQuery(id+"F0.wireOp",VERTEX,"E51.start");
            var Q18;
            Q18=sQuery(id+"F0.wireOp",VERTEX,"E50.start");
            var Q19;
            Q19=sQuery(id+"F0.wireOp",VERTEX,"E22.start");
            var Q20;
            Q20=sQuery(id+"F0.wireOp",VERTEX,"E23.start");
            var Q21;
            Q21=sQuery(id+"F0.wireOp",VERTEX,"E28.end");
            var Q22;
            Q22=makeQuery(id+"F1.opExtrude","SWEPT_BODY",BODY,{"disambiguationData":[OSD([sQuery(id+"F0.wireOp",EDGE,"E34"),sQuery(id+"F0.wireOp",EDGE,"E35"),sQuery(id+"F0.wireOp",EDGE,"E36"),sQuery(id+"F0.wireOp",EDGE,"E37"),sQuery(id+"F0.wireOp",EDGE,"E38"),sQuery(id+"F0.wireOp",EDGE,"E39"),sQuery(id+"F0.wireOp",EDGE,"E40")])]});
            var Q23;
            Q23=makeQuery(id+"F1.opExtrude","SWEPT_BODY",BODY,{"disambiguationData":[OSD([sQuery(id+"F0.wireOp",EDGE,"E0"),sQuery(id+"F0.wireOp",EDGE,"E2"),sQuery(id+"F0.wireOp",EDGE,"E3"),sQuery(id+"F0.wireOp",EDGE,"E4"),sQuery(id+"F0.wireOp",EDGE,"E5"),sQuery(id+"F0.wireOp",EDGE,"E6"),sQuery(id+"F0.wireOp",EDGE,"E8")])]});
            var Q24;
            Q24=makeQuery(id+"F1.opExtrude","SWEPT_BODY",BODY,{"disambiguationData":[OSD([sQuery(id+"F0.wireOp",EDGE,"E29"),sQuery(id+"F0.wireOp",EDGE,"E30"),sQuery(id+"F0.wireOp",EDGE,"E31"),sQuery(id+"F0.wireOp",EDGE,"E32"),sQuery(id+"F0.wireOp",EDGE,"E33")])]});
            var Q25;
            Q25=makeQuery(id+"F1.opExtrude","SWEPT_BODY",BODY,{"disambiguationData":[OSD([sQuery(id+"F0.wireOp",EDGE,"E16"),sQuery(id+"F0.wireOp",EDGE,"E17"),sQuery(id+"F0.wireOp",EDGE,"E18"),sQuery(id+"F0.wireOp",EDGE,"E19"),sQuery(id+"F0.wireOp",EDGE,"E20")])]});
            hole(context, id + "F22", {"style" : HoleStyle.SIMPLE, "endStyle" : HoleEndStyle.THROUGH, "oppositeDirection" : true, "standardTappedOrClearance" : lookupTablePath({ "standard" : "ISO", "fit" : "Normal", "size" : "M5", "type" : "Clearance" }), "standardBlindInLast" : lookupTablePath({ "fit" : "Standard", "standard" : "ISO", "size" : "M5", "type" : "Clearance" }), "holeDiameter" : 5.5 * mm, "locations" : qUnion([Q0, Q1, Q2, Q3, Q4, Q5, Q6, Q7, Q8, Q9, Q10, Q11, Q12, Q13, Q14, Q15, Q16, Q17, Q18, Q19, Q20, Q21]), "scope" : qUnion([Q22, Q23, Q24, Q25]), "isTappedThrough" : true});
        }
        {
            var Q0;
            Q0=makeQuery(id+"F1.opExtrude","CAP_FACE",FACE,{"disambiguationData":[OSD([sQuery(id+"F0.wireOp",EDGE,"E34"),sQuery(id+"F0.wireOp",EDGE,"E35"),sQuery(id+"F0.wireOp",EDGE,"E36"),sQuery(id+"F0.wireOp",EDGE,"E37"),sQuery(id+"F0.wireOp",EDGE,"E38"),sQuery(id+"F0.wireOp",EDGE,"E39"),sQuery(id+"F0.wireOp",EDGE,"E40")])],"isStart":false});
            var sketch = newSketch(context, id + "F23", { "sketchPlane" : qUnion([Q0])});
            skLineSegment(sketch, "E166", {"start": v(-120, -52.93) * mm, "end": v(-105.3, -38.23) * mm});
            skLineSegment(sketch, "E167", {"start": v(-105.3, -38.23) * mm, "end": v(-120, -23.54) * mm});
            skLineSegment(sketch, "E168", {"start": v(-120, -23.54) * mm, "end": v(-120, -52.93) * mm});
            skLineSegment(sketch, "E169", {"start": v(-101.77, -34.7) * mm, "end": v(-116.46, -20) * mm});
            skLineSegment(sketch, "E170", {"start": v(-116.46, -20) * mm, "end": v(-87.07, -20) * mm});
            skLineSegment(sketch, "E171", {"start": v(-87.07, -20) * mm, "end": v(-101.77, -34.7) * mm});
            skLineSegment(sketch, "E172", {"start": v(-120, -23.54) * mm, "end": v(-120, -20) * mm, "construction": true});
            skLineSegment(sketch, "E173", {"start": v(-120, -20) * mm, "end": v(-116.46, -20) * mm, "construction": true});
            skSolve(sketch);
        }
        {
            var Q0;
            Q0=makeQuery(id+"F23.imprint","IMPRINT",FACE,{"disambiguationData":[TD([[makeQuery(id+"F23.imprint","IMPRINT",EDGE,{"derivedFrom":sQuery(id+"F23.wireOp",EDGE,"E166")}),1.0]])]});
            var Q1;
            Q1=makeQuery(id+"F23.imprint","IMPRINT",FACE,{"disambiguationData":[TD([[makeQuery(id+"F23.imprint","IMPRINT",EDGE,{"derivedFrom":sQuery(id+"F23.wireOp",EDGE,"E169")}),-1.0]])]});
            extrude(context, id + "F24", {"entities" : qUnion([Q0, Q1]), "operationType" : NewBodyOperationType.REMOVE, "endBound" : BoundingType.THROUGH_ALL, "oppositeDirection" : true, "depth" : 25 * mm});
        }
        {
            var Q0;
            {var subQ0=sQuery(id+"F0.wireOp",EDGE,"E31");var subQ1=sQuery(id+"F0.wireOp",EDGE,"E30");var subQ2=sQuery(id+"F0.wireOp",EDGE,"E32");var subQ3=sQuery(id+"F0.wireOp",EDGE,"E29");Q0=makeQuery(id+"F15.boolean.opBoolean","SPLIT",FACE,{"disambiguationData":[TD([makeQuery(id+"F1.opExtrude","SWEPT_FACE",FACE,{"disambiguationData":[OSD([subQ1])]})])],"derivedFrom":makeQuery(id+"F1.opExtrude","CAP_FACE",FACE,{"disambiguationData":[OSD([subQ3,subQ1,subQ0,subQ2,sQuery(id+"F0.wireOp",EDGE,"E33")])],"isStart":false})});}
            var sketch = newSketch(context, id + "F25", { "sketchPlane" : qUnion([Q0])});
            skLineSegment(sketch, "E174", {"start": v(-86, -140) * mm, "end": v(-98.2, -121.73) * mm});
            skLineSegment(sketch, "E175", {"start": v(-98.2, -121.73) * mm, "end": v(-116.46, -140) * mm});
            skLineSegment(sketch, "E176", {"start": v(-116.46, -140) * mm, "end": v(-86, -140) * mm});
            skLineSegment(sketch, "E177", {"start": v(-120, -136.46) * mm, "end": v(-120, -89.01) * mm});
            skLineSegment(sketch, "E178", {"start": v(-120, -89.01) * mm, "end": v(-101.02, -117.48) * mm});
            skLineSegment(sketch, "E179", {"start": v(-101.02, -117.48) * mm, "end": v(-120, -136.46) * mm});
            skLineSegment(sketch, "E180", {"start": v(-116.46, -140) * mm, "end": v(-120, -140) * mm, "construction": true});
            skLineSegment(sketch, "E181", {"start": v(-120, -140) * mm, "end": v(-120, -136.46) * mm, "construction": true});
            skSolve(sketch);
        }
        {
            var Q0;
            Q0=makeQuery(id+"F25.imprint","IMPRINT",FACE,{"disambiguationData":[TD([[makeQuery(id+"F25.imprint","IMPRINT",EDGE,{"derivedFrom":sQuery(id+"F25.wireOp",EDGE,"E177")}),-1.0]])]});
            var Q1;
            Q1=makeQuery(id+"F25.imprint","IMPRINT",FACE,{"disambiguationData":[TD([[makeQuery(id+"F25.imprint","IMPRINT",EDGE,{"derivedFrom":sQuery(id+"F25.wireOp",EDGE,"E174")}),1.0]])]});
            extrude(context, id + "F26", {"entities" : qUnion([Q0, Q1]), "operationType" : NewBodyOperationType.REMOVE, "endBound" : BoundingType.THROUGH_ALL, "oppositeDirection" : true, "depth" : 25 * mm});
        }
    });
